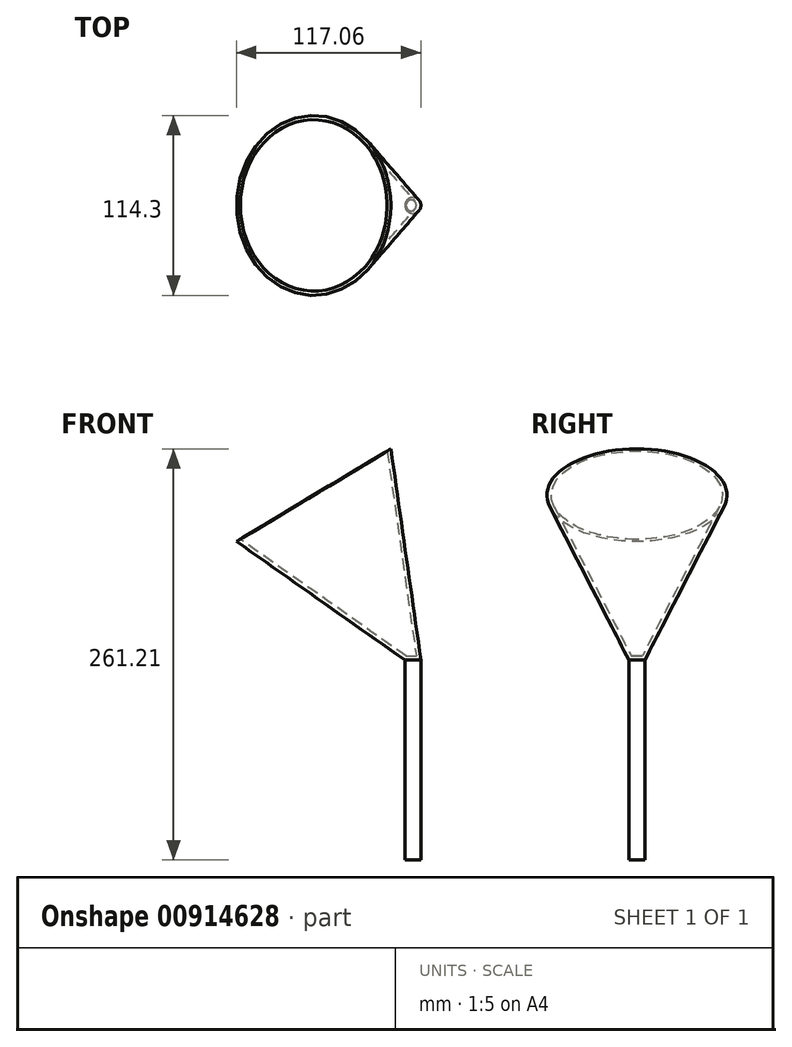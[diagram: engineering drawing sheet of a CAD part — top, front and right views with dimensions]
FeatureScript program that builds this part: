
annotation { "Feature Type Name" : "Feature", "Feature Type Description" : "" }
export const myFeature = defineFeature(function(context is Context, id is Id, definition is map)
    precondition{}
    {
        {
            var Q0;
            Q0=qCreatedBy(makeId("Top.planeOp"),FACE);
            var sketch = newSketch(context, id + "F0", { "sketchPlane" : qUnion([Q0])});
            skCircle(sketch, "E0", {"center": v(0, 0) * mm, "radius": 5.08 * mm});
            skSolve(sketch);
        }
        {
            var Q0;
            Q0 = qSketchRegion(id + "F0", true);
            extrude(context, id + "F1", {"entities" : qUnion([Q0]), "depth" : 127 * mm, "offsetDistance" : 25.4 * mm});
        }
        {
            var Q0;
            Q0=qCreatedBy(makeId("Front.planeOp"),FACE);
            var sketch = newSketch(context, id + "F2", { "sketchPlane" : qUnion([Q0])});
            skLineSegment(sketch, "E1", {"start": v(0, 127.63) * mm, "end": v(-62.7, 231.95) * mm});
            skSolve(sketch);
        }
        {
            var Q0;
            Q0=sQuery(id+"F2.wireOp",EDGE,"E1");
            var Q1;
            Q1=sQuery(id+"F2.wireOp",VERTEX,"E1.end");
            cPlane(context, id + "F3", {"entities" : qUnion([Q0, Q1]), "cplaneType" : CPlaneType.CURVE_POINT, "offset" : 25.4 * mm, "width" : 152.4 * mm, "height" : 152.4 * mm});
        }
        {
            var Q0;
            Q0=qCreatedBy(id+"F3.planeOp",FACE);
            var sketch = newSketch(context, id + "F4", { "sketchPlane" : qUnion([Q0])});
            skCircle(sketch, "E2", {"center": v(65.4, 0) * mm, "radius": 57.15 * mm});
            skSolve(sketch);
        }
        {
            var Q0;
            Q0=makeQuery(id+"F1.opExtrude","CAP_FACE",FACE,{"disambiguationData":[OSD([sQuery(id+"F0.wireOp",EDGE,"E0")])],"isStart":false});
            var Q1;
            Q1=makeQuery(id+"F4.imprint","IMPRINT",FACE,{"disambiguationData":[TD([[makeQuery(id+"F4.imprint","IMPRINT",EDGE,{"derivedFrom":sQuery(id+"F4.wireOp",EDGE,"E2")}),1.0]])]});
            loft(context, id + "F5", {"sheetProfilesArray" : [{ "sheetProfileEntities" : qUnion([Q0]) }, { "sheetProfileEntities" : qUnion([Q1]) }]});
        }
        {
            var Q0;
            Q0=makeQuery(id+"F5.opLoft","CAP_FACE",FACE,{"disambiguationData":[OSD([makeQuery(id+"F4.imprint","IMPRINT",FACE,{"disambiguationData":[TD([[makeQuery(id+"F4.imprint","IMPRINT",EDGE,{"derivedFrom":sQuery(id+"F4.wireOp",EDGE,"E2")}),1.0]])]})])],"isStart":true});
            shell(context, id + "F6", {"entities" : qUnion([Q0]), "thickness" : 2.54 * mm});
        }
    });
